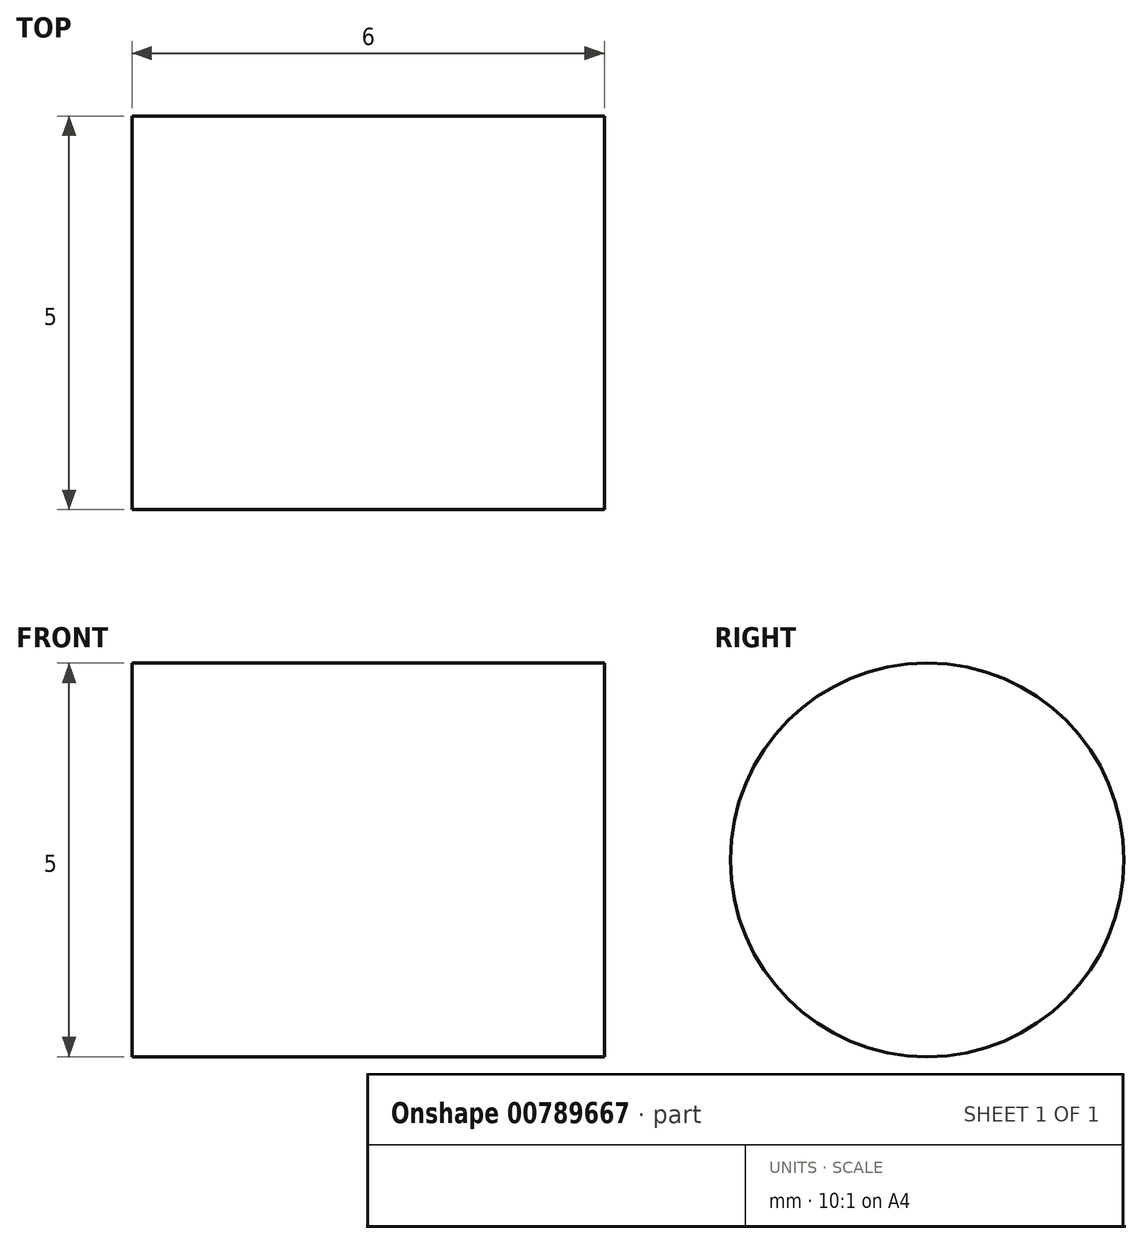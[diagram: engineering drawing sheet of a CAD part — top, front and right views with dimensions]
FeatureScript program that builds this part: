
annotation { "Feature Type Name" : "Feature", "Feature Type Description" : "" }
export const myFeature = defineFeature(function(context is Context, id is Id, definition is map)
    precondition{}
    {
        {
            var Q0;
            Q0=qCreatedBy(makeId("Right.planeOp"),FACE);
            var sketch = newSketch(context, id + "F0", { "sketchPlane" : qUnion([Q0])});
            skCircle(sketch, "E0", {"center": v(0, 0) * mm, "radius": 2.5 * mm});
            skSolve(sketch);
        }
        {
            var Q0;
            Q0=makeQuery(id+"F0.imprint","IMPRINT",FACE,{"disambiguationData":[TD([[makeQuery(id+"F0.imprint","IMPRINT",EDGE,{"derivedFrom":sQuery(id+"F0.wireOp",EDGE,"E0")}),1.0]])]});
            extrude(context, id + "F1", {"entities" : qUnion([Q0]), "depth" : 6 * mm, "offsetDistance" : 25 * mm});
        }
    });
